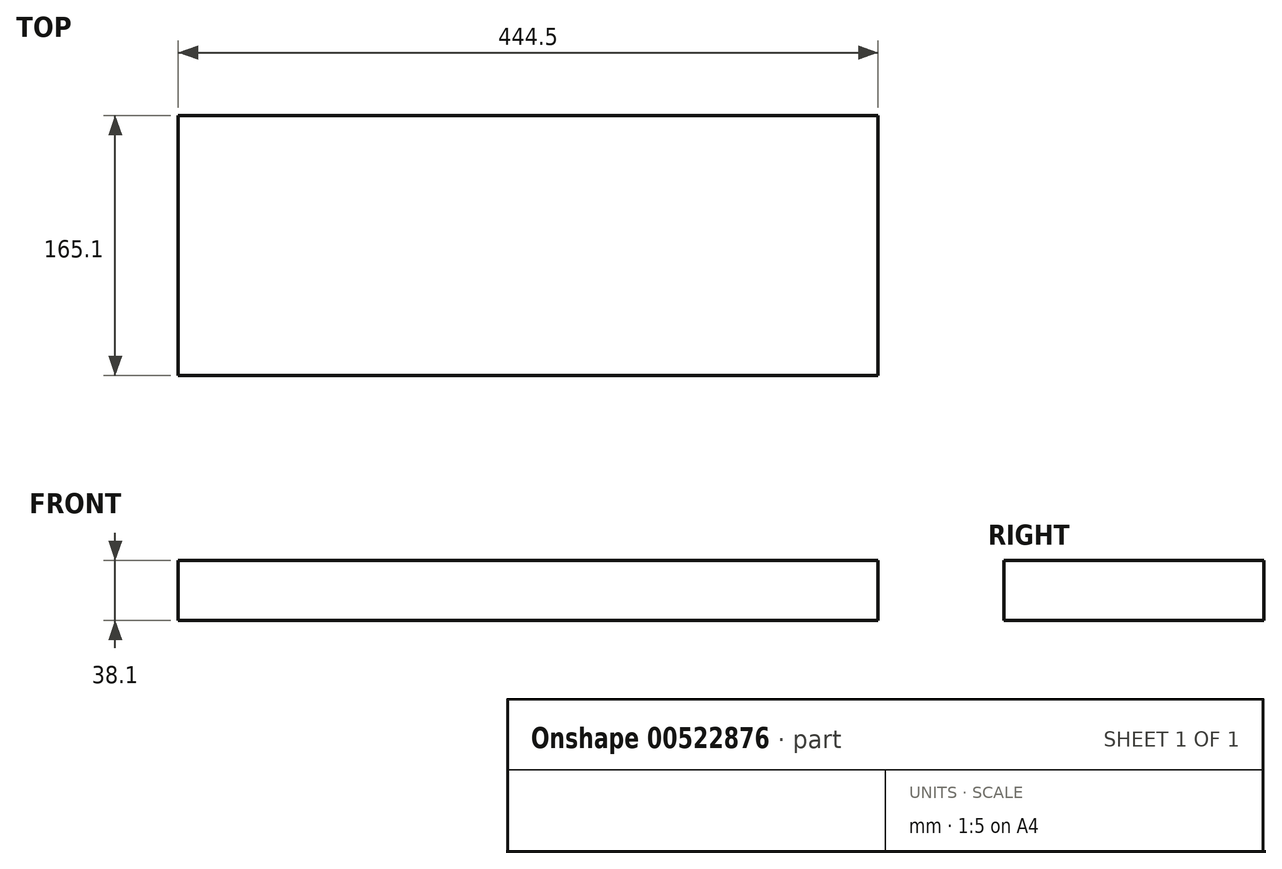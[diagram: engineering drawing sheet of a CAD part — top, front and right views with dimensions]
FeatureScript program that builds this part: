
annotation { "Feature Type Name" : "Feature", "Feature Type Description" : "" }
export const myFeature = defineFeature(function(context is Context, id is Id, definition is map)
    precondition{}
    {
        {
            var Q0;
            Q0=qCreatedBy(makeId("Top.planeOp"),FACE);
            var sketch = newSketch(context, id + "F0", { "sketchPlane" : qUnion([Q0])});
            skLineSegment(sketch, "E0.bottom", {"start": v(-222.25, 82.55) * mm, "end": v(222.25, 82.55) * mm});
            skLineSegment(sketch, "E0.top", {"start": v(-222.25, -82.55) * mm, "end": v(222.25, -82.55) * mm});
            skLineSegment(sketch, "E0.left", {"start": v(-222.25, 82.55) * mm, "end": v(-222.25, -82.55) * mm});
            skLineSegment(sketch, "E0.right", {"start": v(222.25, 82.55) * mm, "end": v(222.25, -82.55) * mm});
            skPoint(sketch, "E0.middle", {"position": v(0, 0) * mm});
            skSolve(sketch);
        }
        {
            var Q0;
            Q0=makeQuery(id+"F0.imprint","IMPRINT",FACE,{"disambiguationData":[TD([[makeQuery(id+"F0.imprint","IMPRINT",EDGE,{"derivedFrom":sQuery(id+"F0.wireOp",EDGE,"E0.bottom")}),-1.0]])]});
            extrude(context, id + "F1", {"entities" : qUnion([Q0]), "depth" : 38.1 * mm, "offsetDistance" : 25 * mm});
        }
    });
